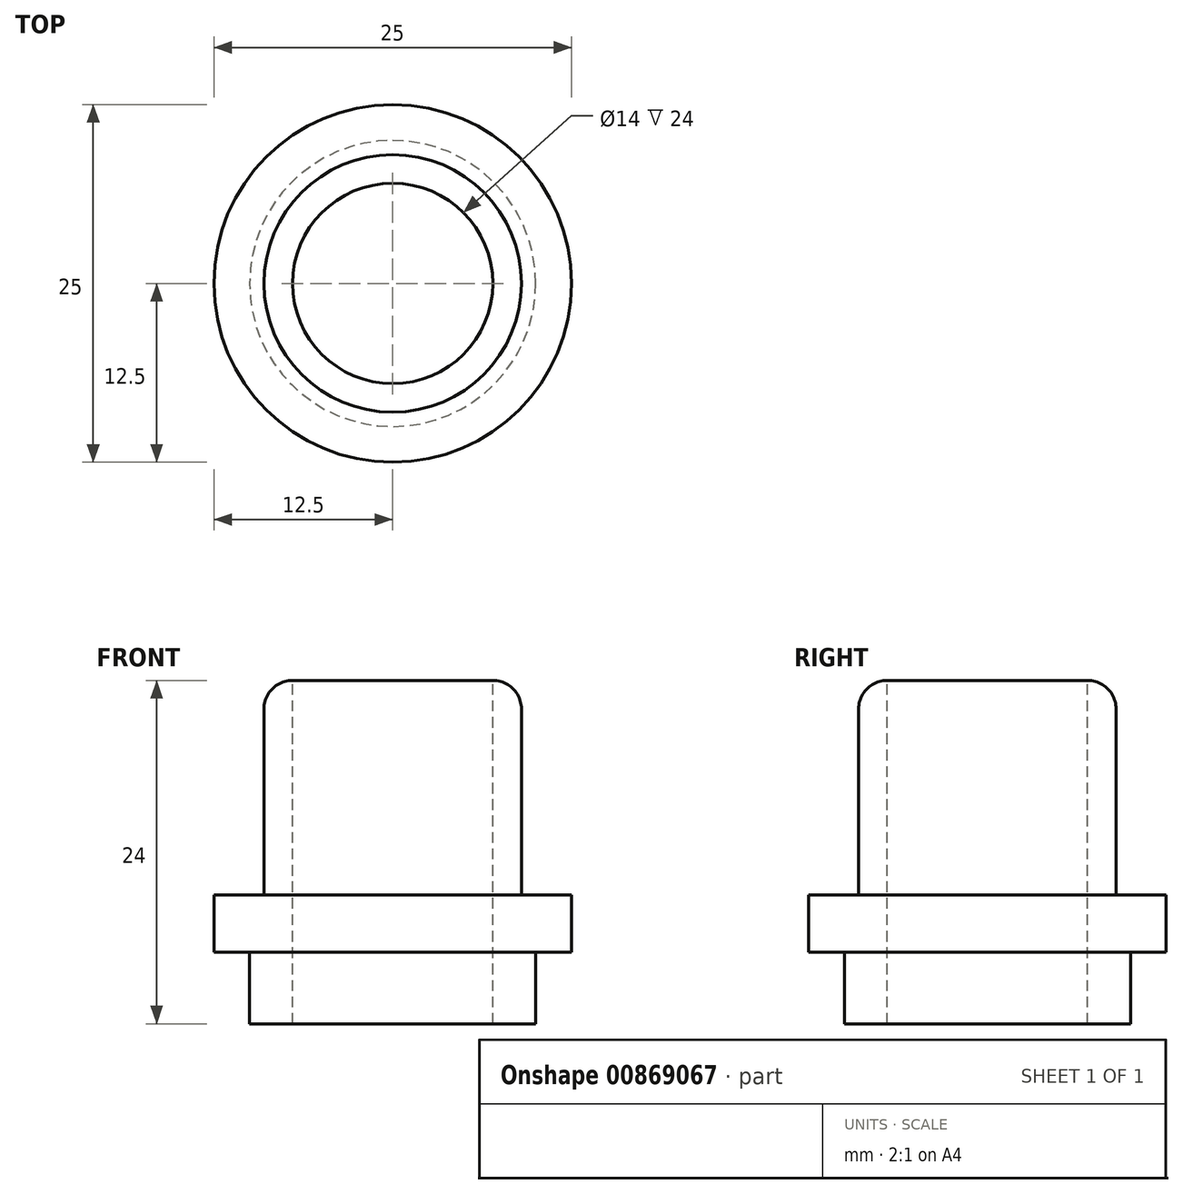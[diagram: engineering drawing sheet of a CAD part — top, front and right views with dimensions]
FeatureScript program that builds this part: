
annotation { "Feature Type Name" : "Feature", "Feature Type Description" : "" }
export const myFeature = defineFeature(function(context is Context, id is Id, definition is map)
    precondition{}
    {
        {
            var Q0;
            Q0=qCreatedBy(makeId("Front.planeOp"),FACE);
            var sketch = newSketch(context, id + "F0", { "sketchPlane" : qUnion([Q0])});
            skLineSegment(sketch, "E0.bottom", {"start": v(0, 15) * mm, "end": v(9, 15) * mm});
            skLineSegment(sketch, "E0.top", {"start": v(0, 0) * mm, "end": v(9, 0) * mm});
            skLineSegment(sketch, "E0.left", {"start": v(0, 15) * mm, "end": v(0, 0) * mm});
            skLineSegment(sketch, "E0.right", {"start": v(9, 15) * mm, "end": v(9, 0) * mm});
            skLineSegment(sketch, "E1.bottom", {"start": v(0, 0) * mm, "end": v(12.5, 0) * mm});
            skLineSegment(sketch, "E1.top", {"start": v(0, -4) * mm, "end": v(12.5, -4) * mm});
            skLineSegment(sketch, "E1.left", {"start": v(0, 0) * mm, "end": v(0, -4) * mm});
            skLineSegment(sketch, "E1.right", {"start": v(12.5, 0) * mm, "end": v(12.5, -4) * mm});
            skLineSegment(sketch, "E2.bottom", {"start": v(0, -4) * mm, "end": v(10, -4) * mm});
            skLineSegment(sketch, "E2.top", {"start": v(0, -9) * mm, "end": v(10, -9) * mm});
            skLineSegment(sketch, "E2.left", {"start": v(0, -4) * mm, "end": v(0, -9) * mm});
            skLineSegment(sketch, "E2.right", {"start": v(10, -4) * mm, "end": v(10, -9) * mm});
            skLineSegment(sketch, "E3", {"start": v(7, 15) * mm, "end": v(7, -9) * mm});
            skSolve(sketch);
        }
        {
            var Q0;
            {var subQ0=sQuery(id+"F0.wireOp",EDGE,"E0.right");Q0=makeQuery(id+"F0.imprint","IMPRINT",FACE,{"disambiguationData":[TD([[makeQuery(id+"F0.imprint","IMPRINT",EDGE,{"derivedFrom":subQ0}),-1.0]])]});}
            var Q1;
            {var subQ1=sQuery(id+"F0.wireOp",EDGE,"E1.top");Q1=makeQuery(id+"F0.imprint","IMPRINT",FACE,{"disambiguationData":[TD([[makeQuery(id+"F0.imprint","IMPRINT",EDGE,{"derivedFrom":subQ1}),1.0]])]});}
            var Q2;
            {var subQ0=sQuery(id+"F0.wireOp",EDGE,"E2.right");Q2=makeQuery(id+"F0.imprint","IMPRINT",FACE,{"disambiguationData":[TD([[makeQuery(id+"F0.imprint","IMPRINT",EDGE,{"derivedFrom":subQ0}),-1.0]])]});}
            var Q3;
            Q3=sQuery(id+"F0.wireOp",EDGE,"E0.left");
            revolve(context, id + "F1", {"surfaceOperationType" : NewSurfaceOperationType.NEW, "entities" : qUnion([Q0, Q1, Q2]), "axis" : qUnion([Q3]), "revolveType" : RevolveType.FULL});
        }
        {
            var Q0;
            Q0=makeQuery(id+"F1.opRevolve","SWEPT_EDGE",EDGE,{"disambiguationData":[OSD([sQuery(id+"F0.wireOp",EDGE,"E0.bottom"),sQuery(id+"F0.wireOp",EDGE,"E0.right")])]});
            fillet(context, id + "F2", {"entities" : qUnion([Q0]), "radius" : 2 * mm, "tangentPropagation" : true, "allowEdgeOverflow" : false});
        }
    });
